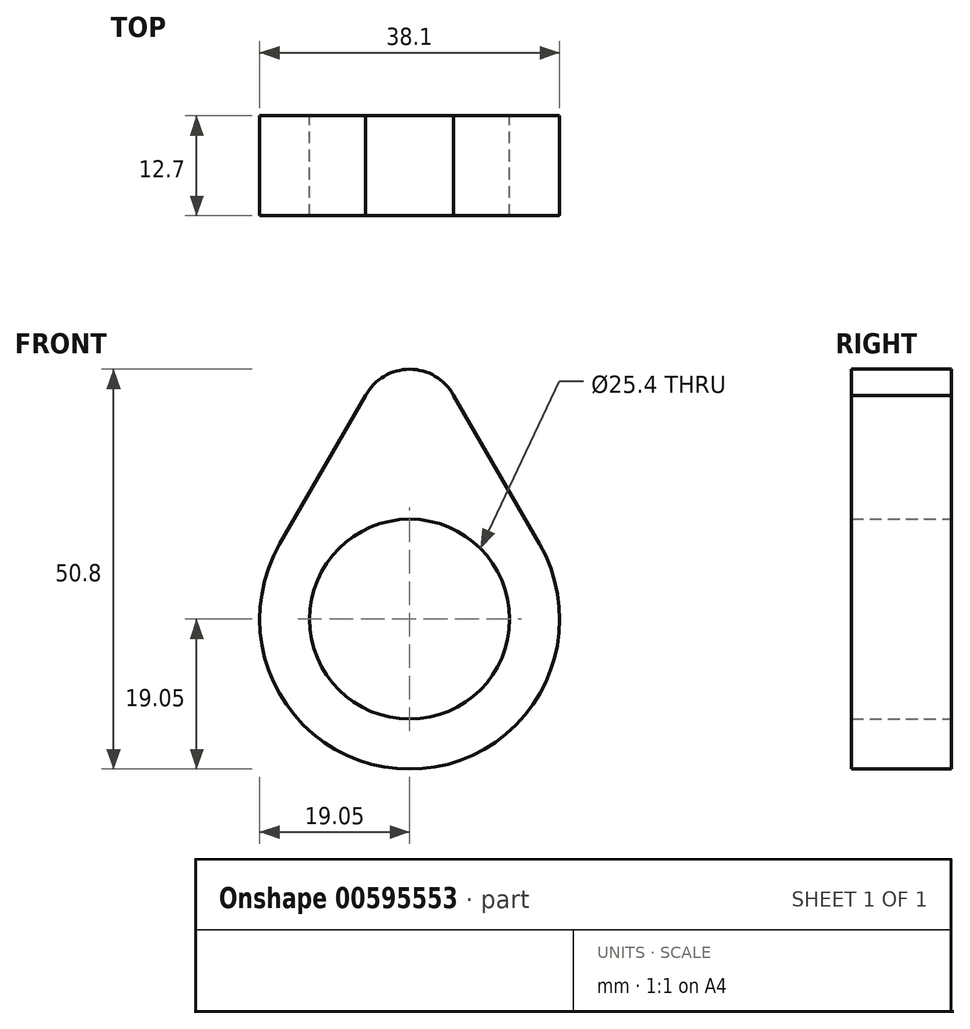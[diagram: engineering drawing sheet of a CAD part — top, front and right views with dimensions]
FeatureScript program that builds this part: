
annotation { "Feature Type Name" : "Feature", "Feature Type Description" : "" }
export const myFeature = defineFeature(function(context is Context, id is Id, definition is map)
    precondition{}
    {
        {
            var Q0;
            Q0=qCreatedBy(makeId("Front.planeOp"),FACE);
            var sketch = newSketch(context, id + "F0", { "sketchPlane" : qUnion([Q0])});
            skCircle(sketch, "E0", {"center": v(0, 0) * mm, "radius": 12.7 * mm});
            skArc(sketch, "E1", {"start": v(5.58, 28.43) * mm, "mid": v(0, 31.75) * mm, "end": v(-5.58, 28.43) * mm});
            skArc(sketch, "E2", {"start": v(-16.5, 9.53) * mm, "mid": v(0, -19.05) * mm, "end": v(16.5, 9.53) * mm});
            skLineSegment(sketch, "E3", {"start": v(-5.58, 28.43) * mm, "end": v(-16.5, 9.53) * mm});
            skLineSegment(sketch, "E4", {"start": v(5.58, 28.43) * mm, "end": v(16.5, 9.53) * mm});
            skSolve(sketch);
        }
        {
            var Q0;
            Q0=makeQuery(id+"F0.imprint","IMPRINT",FACE,{"disambiguationData":[TD([[makeQuery(id+"F0.imprint","IMPRINT",EDGE,{"derivedFrom":sQuery(id+"F0.wireOp",EDGE,"E0")}),-1.0]])]});
            extrude(context, id + "F1", {"entities" : qUnion([Q0]), "depth" : 12.7 * mm, "offsetDistance" : 25.4 * mm, "symmetric" : true});
        }
    });
